# Revit family: ASH_ArmitageShanks_WallHungHandRinseBasins_Contour21-37cm
name_source: partatom
category: Plumbing Fixtures
revit_build: Autodesk Revit MEP 2012 (Build: 20110309_2315(x64)
units: mm (PartAtom-declared; Revit-internal decimal feet)

## types (3) — shared parameters
AccessibilityPerformance = DDA Compliant
Accessories = www.idealspec.co.uk
AreaUnits = millimeters
Assembly Code = C1030200
AssetType = Fixed
Brand = Armitage Shanks
Category = SanitaryTerminal_WASHHANDBASIN_UK
Color = White
ConnectionType = Plumbing
Default Elevation = 730 mm  [stored 2.39501 ft]
DrainSize = 32 mm  [stored 0.104987 ft]
DurationUnit = year
ExpectedLife = 30
Finish = White
IfcExportAs = IfcSanitaryTerminalType
IfcExportType = WASHHANDBASIN
InstallationInstructions = www.idealspec.co.uk/resources.html
LinearUnits = millimeters
ManufacturerURL = www.idealspec.co.uk
Material = Vitreous china
NBSDescription = Wall hung hand rinse basins
NBSReference = 35-70-70/368
NettWeight = 8.2 Kg
NominalDepth = 306 mm
NominalHeight = 170 mm
NominalLength = 306 mm
NominalWidth = 370 mm
S8810AAStrainerWasteUnslotted = Yes
S911067ConcealedHangers = Yes
Shape = Sculptured
Size = 370 x 306 x 170 mm
Space = Internal
SpareParts = www.fastpart-spares.co.uk
URL = www.idealspec.co.uk
Uniclass2 = Pr_40_20_96_95
Version = 1
VolumeUnits = Litres
WarrantyDescription = Manufacturers warranty
WarrantyDurationParts = 99
WarrantyDurationUnit = year
WashHandBasinMounting = Wall hung
WashHandBasinType = HANDRINSE
zero-valued in all types: CWFU, HWFU, WFU

## per-type parameters (varying)
| type | BIMObjectName | BasinMaterial | CentreTap | Description | ECA | Features | LHTap | Model | ModelNumber | ModelReference | Name | ProductInformation | RHTap | S212201Plan | S247301Plan | S247401Plan | WRAS | WaterEfficientProduct |
| S247301 Contour 21 37cm handrinse washbasin left hand taphole | ASH_ArmitageShanks_WallHungHandRinseBasins_Contour21_S2473 | <By Category> | No | Contour 21 37 cm handrinse washbasin left hand taphole no overflow or chainstay hole, bottom outlet | No | Left hand taphole no overflow or chainstay hole, bottom outlet | Yes | S247301 | S247301 | Contour 21 37 cm handrinse washbasin left hand taphole no overflow or chainstay hole, bottom outlet | WallHungHandRinseBasins_Contour21_S2473_ArmitageShanks | www.idealspec.co.uk/assets/datasheet/S247301 | No | No | Yes | No | No | No |
| S247401 Contour 21 37cm handrinse washbasin Right hand taphole | ASH_ArmitageShanks_WallHungHandRinseBasins_Contour21_S2474 | ASH_ArmitageShanks _Sanitaryware_White4_Render | No | Contour 21 37 cm handrinse washbasin right hand taphole no overflow or chainstay hole, bottom outlet | Yes | Right hand taphole no overflow or chainstay hole, bottom outlet | No | S247401 | S247401 | Contour 21 37 cm handrinse washbasin right hand taphole no overflow or chainstay hole, bottom outlet | WallHungHandRinseBasins_Contour21_S2474_ArmitageShanks | www.idealspec.co.uk/assets/datasheet/S247401 | Yes | No | No | Yes | Yes | Yes |
| S212201 Contour 21 37cm handrinse washbasin Central taphole | ASH_ArmitageShanks_WallHungHandRinseBasins_Contour21_S2122 | <By Category> | Yes | Contour 21 37 cm handrinse washbasin central taphole no overflow or chainstay hole, bottom outlet | No | Central taphole no overflow or chainstay hole, bottom outlet | No | S212201 | S212201 | Contour 21 37 cm handrinse washbasin central taphole no overflow or chainstay hole, bottom outlet | WallHungHandRinseBasins_Contour21_S2122_ArmitageShanks | www.idealspec.co.uk/assets/datasheet/S212201 | No | Yes | No | No | No | No |

note: [stored X ft] marks values corroborated as IEEE doubles in the binary element streams (Revit-internal decimal feet)

## geometry (parser evidence)
native form markers: Sweep x11
no freeform markers — native parametric forms only
